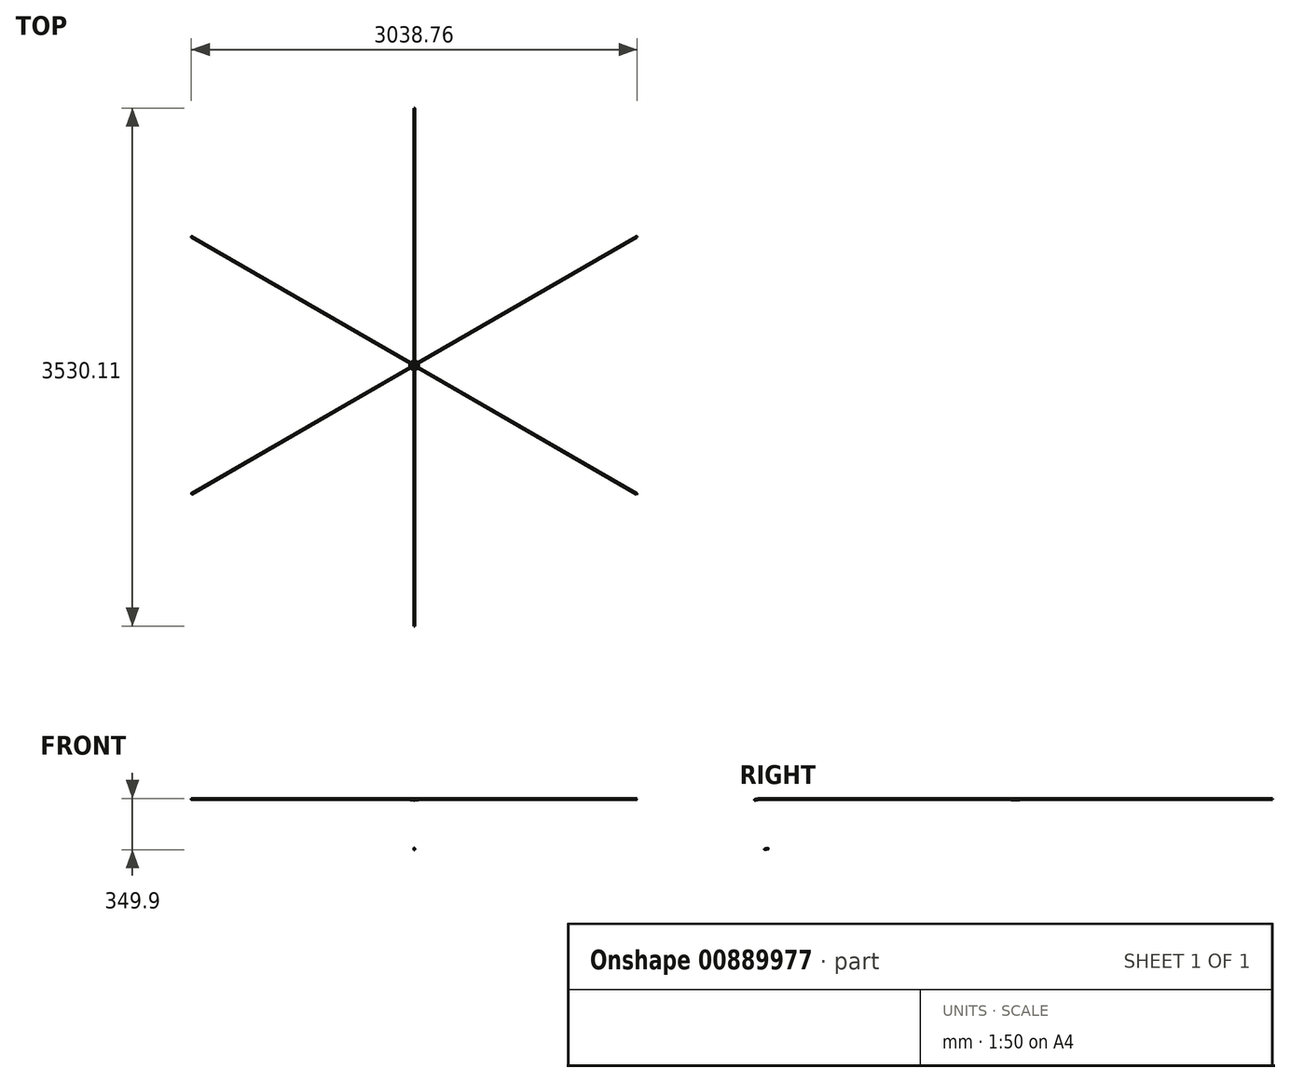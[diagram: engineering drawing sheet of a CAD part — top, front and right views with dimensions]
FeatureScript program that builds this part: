
annotation { "Feature Type Name" : "Feature", "Feature Type Description" : "" }
export const myFeature = defineFeature(function(context is Context, id is Id, definition is map)
    precondition{}
    {
        {
            var Q0;
            Q0=qCreatedBy(makeId("Front.planeOp"),FACE);
            var sketch = newSketch(context, id + "F0", { "sketchPlane" : qUnion([Q0])});
            skCircle(sketch, "E0", {"center": v(25.4, 0) * mm, "radius": 4.76 * mm});
            skLineSegment(sketch, "E1", {"start": v(0, -34.62) * mm, "end": v(0, 31.87) * mm, "construction": true});
            skSolve(sketch);
        }
        {
            var Q0;
            Q0=makeQuery(id+"F0.imprint","IMPRINT",FACE,{"disambiguationData":[TD([[makeQuery(id+"F0.imprint","IMPRINT",EDGE,{"derivedFrom":sQuery(id+"F0.wireOp",EDGE,"E0")}),1.0]])]});
            var Q1;
            Q1=sQuery(id+"F0.wireOp",EDGE,"E1");
            revolve(context, id + "F1", {"surfaceOperationType" : NewSurfaceOperationType.NEW, "entities" : qUnion([Q0]), "axis" : qUnion([Q1]), "revolveType" : RevolveType.FULL});
        }
        {
            var Q0;
            Q0=qCreatedBy(makeId("Front.planeOp"),FACE);
            var sketch = newSketch(context, id + "F2", { "sketchPlane" : qUnion([Q0])});
            skCircle(sketch, "E2", {"center": v(0, 0) * mm, "radius": 3.18 * mm});
            skLineSegment(sketch, "E3", {"start": v(0, 0) * mm, "end": v(0, 32.48) * mm});
            skSolve(sketch);
        }
        {
            var Q0;
            Q0=makeQuery(id+"F2.imprint","IMPRINT",FACE,{"disambiguationData":[TD([[makeQuery(id+"F2.imprint","IMPRINT",EDGE,{"derivedFrom":sQuery(id+"F2.wireOp",EDGE,"E2")}),1.0]])]});
            extrude(context, id + "F3", {"entities" : qUnion([Q0]), "operationType" : NewBodyOperationType.ADD, "oppositeDirection" : true, "depth" : 1752.6 * mm, "offsetDistance" : 25.4 * mm});
        }
        {
            var Q0;
            Q0=qCreatedBy(makeId("Right.planeOp"),FACE);
            var sketch = newSketch(context, id + "F4", { "sketchPlane" : qUnion([Q0])});
            skLineSegment(sketch, "E4", {"start": v(0, 0) * mm, "end": v(0, 37.68) * mm});
            skSolve(sketch);
        }
        {
            var Q0;
            Q0=makeQuery(id+"F1.opRevolve","SWEPT_BODY",BODY,{"disambiguationData":[OSD([sQuery(id+"F0.wireOp",EDGE,"E0")])]});
            var Q1;
            Q1=sQuery(id+"F4.wireOp",EDGE,"E4");
            circularPattern(context, id + "F5", {"operationType" : NewBodyOperationType.ADD, "entities" : qUnion([Q0]), "axis" : qUnion([Q1]), "angle" : 360 * degree, "instanceCount" : 6, "equalSpace" : true, "isCentered" : true});
        }
        {
            var Q0;
            Q0=makeQuery(id+"F5.opPattern","COPY",FACE,{"derivedFrom":makeQuery(id+"F3.opExtrude","CAP_FACE",FACE,{"disambiguationData":[OSD([sQuery(id+"F2.wireOp",EDGE,"E2")])],"isStart":false}),"instanceName":"-3"});
            var sketch = newSketch(context, id + "F6", { "sketchPlane" : qUnion([Q0])});
            skLineSegment(sketch, "E5", {"start": v(-7.27, 0) * mm, "end": v(7.04, 0) * mm});
            skSolve(sketch);
        }
        {
            var Q0;
            Q0=sQuery(id+"F6.wireOp",EDGE,"E5");
            cPlane(context, id + "F7", {"entities" : qUnion([Q0]), "cplaneType" : CPlaneType.LINE_ANGLE, "offset" : 25.4 * mm, "angle" : 11.3 * degree, "width" : 152.4 * mm, "height" : 152.4 * mm});
        }
        {
            var Q0;
            Q0=qCreatedBy(id+"F7.planeOp",FACE);
            var sketch = newSketch(context, id + "F8", { "sketchPlane" : qUnion([Q0])});
            skCircle(sketch, "E6", {"center": v(0, 0) * mm, "radius": 3.17 * mm});
            skSolve(sketch);
        }
        {
            var Q0;
            Q0 = qSketchRegion(id + "F8", true);
            var Q1;
            {var subQ0=sQuery(id+"F6.wireOp",EDGE,"E5");var subQ1=makeQuery(id+"F5.opPattern","COPY",EDGE,{"derivedFrom":makeQuery(id+"F3.opExtrude","CAP_EDGE",EDGE,{"disambiguationData":[OSD([sQuery(id+"F2.wireOp",EDGE,"E2")])],"isStart":false}),"instanceName":"-3"});var subQ2=makeQuery(id+"F6.imprint","INTERSECT",VERTEX,{"disambiguationData":[OD(0.0)],"derivedFrom":[subQ1,subQ0]});Q1=makeQuery(id+"F6.imprint","IMPRINT",FACE,{"disambiguationData":[TD([[makeQuery(id+"F6.imprint","IMPRINT",EDGE,{"disambiguationData":[TD([[subQ2,-1.0]])],"derivedFrom":subQ0}),-1.0]])]});}
            var Q2;
            {var subQ0=sQuery(id+"F6.wireOp",EDGE,"E5");var subQ1=makeQuery(id+"F5.opPattern","COPY",EDGE,{"derivedFrom":makeQuery(id+"F3.opExtrude","CAP_EDGE",EDGE,{"disambiguationData":[OSD([sQuery(id+"F2.wireOp",EDGE,"E2")])],"isStart":false}),"instanceName":"-3"});var subQ2=makeQuery(id+"F6.imprint","INTERSECT",VERTEX,{"disambiguationData":[OD(0.0)],"derivedFrom":[subQ1,subQ0]});Q2=makeQuery(id+"F6.imprint","IMPRINT",FACE,{"disambiguationData":[TD([[makeQuery(id+"F6.imprint","IMPRINT",EDGE,{"disambiguationData":[TD([[subQ2,-1.0]])],"derivedFrom":subQ0}),1.0]])]});}
            extrude(context, id + "F9", {"entities" : qUnion([Q0, Q1, Q2]), "operationType" : NewBodyOperationType.ADD, "oppositeDirection" : true, "depth" : 25.4 * mm, "offsetDistance" : 25.4 * mm});
        }
    });
